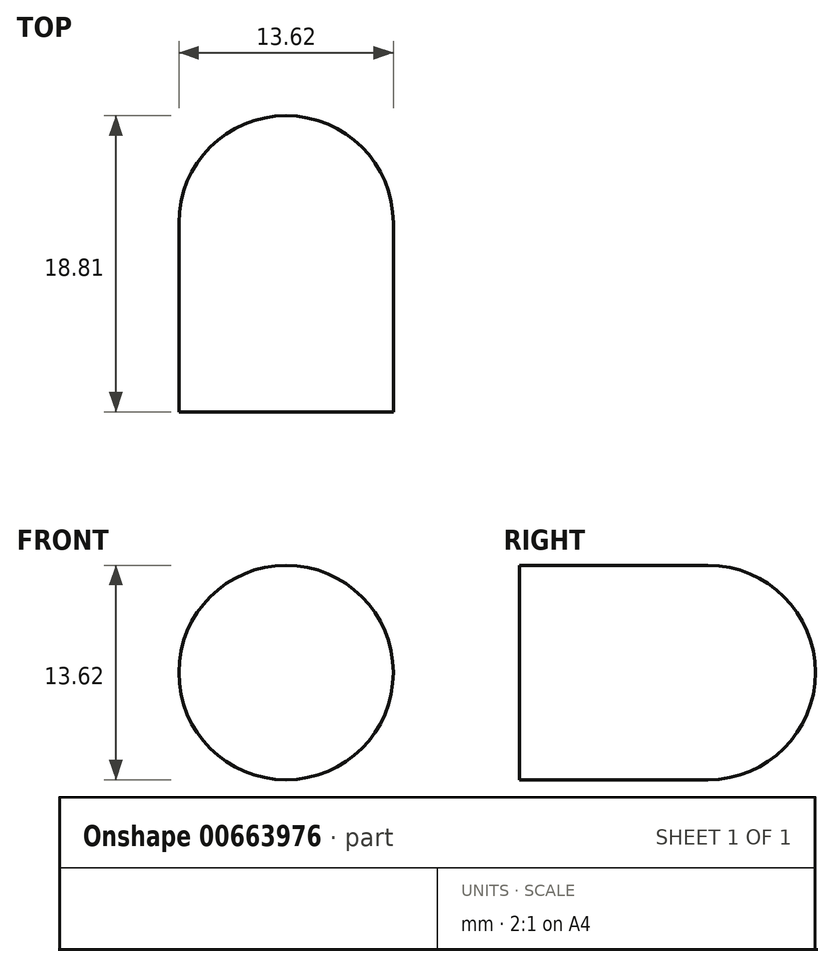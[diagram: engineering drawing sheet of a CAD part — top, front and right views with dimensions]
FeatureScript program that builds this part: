
annotation { "Feature Type Name" : "Feature", "Feature Type Description" : "" }
export const myFeature = defineFeature(function(context is Context, id is Id, definition is map)
    precondition{}
    {
        {
            var Q0;
            Q0=qCreatedBy(makeId("Front.planeOp"),FACE);
            var sketch = newSketch(context, id + "F0", { "sketchPlane" : qUnion([Q0])});
            skCircle(sketch, "E0", {"center": v(0, 0) * mm, "radius": 6.81 * mm});
            skSolve(sketch);
        }
        {
            var Q0;
            Q0 = qSketchRegion(id + "F0", true);
            extrude(context, id + "F1", {"entities" : qUnion([Q0]), "depth" : 12 * mm, "offsetDistance" : 25 * mm});
        }
        {
            var Q0;
            Q0=makeQuery(id+"F1.opExtrude","CAP_FACE",FACE,{"disambiguationData":[OSD([sQuery(id+"F0.wireOp",EDGE,"E0")])],"isStart":true});
            var sketch = newSketch(context, id + "F2", { "sketchPlane" : qUnion([Q0])});
            skCircle(sketch, "E1", {"center": v(0, 0) * mm, "radius": 6.81 * mm});
            skLineSegment(sketch, "E2", {"start": v(0, 6.81) * mm, "end": v(0, -6.81) * mm});
            skSolve(sketch);
        }
        {
            var Q0;
            {var subQ0=sQuery(id+"F2.wireOp",EDGE,"E2");Q0=makeQuery(id+"F2.imprint","IMPRINT",FACE,{"disambiguationData":[TD([[makeQuery(id+"F2.imprint","IMPRINT",EDGE,{"derivedFrom":subQ0}),-1.0]])]});}
            var Q1;
            Q1=sQuery(id+"F2.wireOp",EDGE,"E2");
            revolve(context, id + "F3", {"operationType" : NewBodyOperationType.ADD, "entities" : qUnion([Q0]), "axis" : qUnion([Q1]), "revolveType" : RevolveType.FULL});
        }
    });
